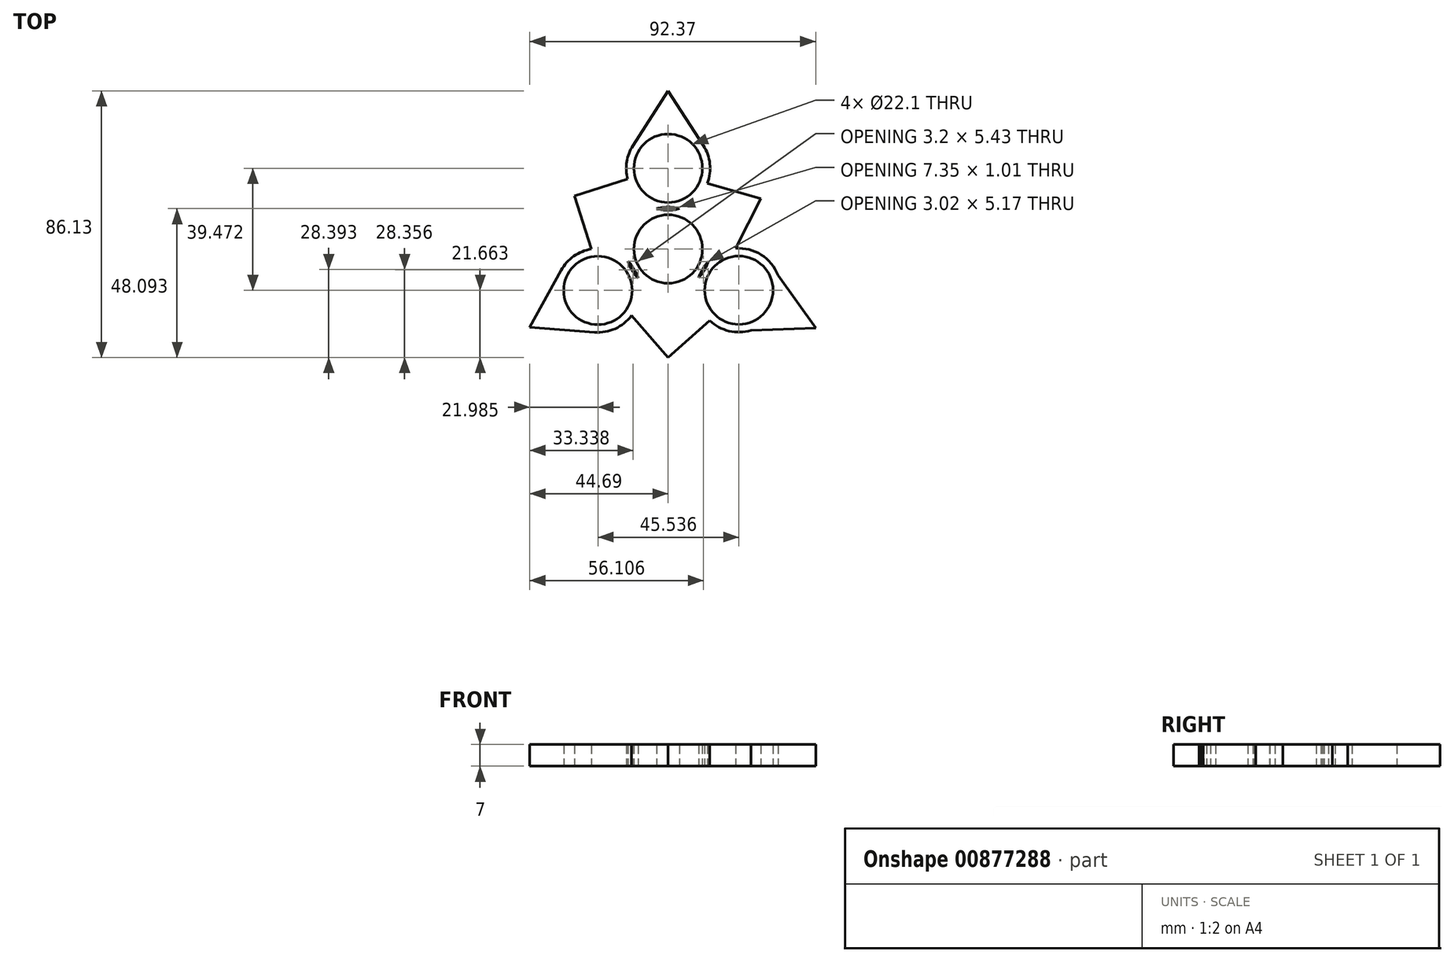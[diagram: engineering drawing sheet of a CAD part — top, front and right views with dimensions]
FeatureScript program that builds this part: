
annotation { "Feature Type Name" : "Feature", "Feature Type Description" : "" }
export const myFeature = defineFeature(function(context is Context, id is Id, definition is map)
    precondition{}
    {
        {
            var Q0;
            Q0=qCreatedBy(makeId("Top.planeOp"),FACE);
            var sketch = newSketch(context, id + "F0", { "sketchPlane" : qUnion([Q0])});
            skCircle(sketch, "E0", {"center": v(0, 0) * mm, "radius": 11.05 * mm});
            skCircle(sketch, "E1", {"center": v(0, 0) * mm, "radius": 13.55 * mm});
            skCircle(sketch, "E2", {"center": v(0, 26.09) * mm, "radius": 11.05 * mm});
            skCircle(sketch, "E3", {"center": v(0, 26.09) * mm, "radius": 13.55 * mm});
            skCircle(sketch, "E4.1.0", {"center": v(-22.7, -13.39) * mm, "radius": 11.05 * mm});
            skCircle(sketch, "E4.1.1", {"center": v(-22.7, -13.39) * mm, "radius": 13.55 * mm});
            skPoint(sketch, "E4.center", {"position": v(0.04, -0.2) * mm});
            skCircle(sketch, "E5.1.2.0", {"center": v(22.83, -13.31) * mm, "radius": 11.05 * mm});
            skCircle(sketch, "E5.2.2.0", {"center": v(22.83, -13.31) * mm, "radius": 13.55 * mm});
            skLineSegment(sketch, "E6", {"start": v(-11.39, 33.43) * mm, "end": v(0, 51.08) * mm});
            skLineSegment(sketch, "E7", {"start": v(0, 51.08) * mm, "end": v(11.39, 33.43) * mm});
            skLineSegment(sketch, "E8", {"start": v(-44.69, -25.27) * mm, "end": v(-34.58, -6.86) * mm});
            skLineSegment(sketch, "E9", {"start": v(-44.69, -25.27) * mm, "end": v(-23.75, -26.9) * mm});
            skLineSegment(sketch, "E10", {"start": v(-11.86, -21.5) * mm, "end": v(0, -35.05) * mm});
            skLineSegment(sketch, "E11", {"start": v(0, -35.05) * mm, "end": v(13.46, -23.1) * mm});
            skLineSegment(sketch, "E12", {"start": v(35.49, -8.47) * mm, "end": v(47.68, -25.56) * mm});
            skLineSegment(sketch, "E13", {"start": v(47.68, -25.56) * mm, "end": v(26.7, -26.3) * mm});
            skLineSegment(sketch, "E14", {"start": v(21.8, 0.2) * mm, "end": v(29.95, 16.24) * mm});
            skLineSegment(sketch, "E15", {"start": v(29.95, 16.24) * mm, "end": v(12.66, 21.25) * mm});
            skLineSegment(sketch, "E16", {"start": v(-24.8, 0) * mm, "end": v(-30.25, 17.16) * mm});
            skLineSegment(sketch, "E17", {"start": v(-30.25, 17.16) * mm, "end": v(-13.1, 22.6) * mm});
            skSolve(sketch);
        }
        {
            var Q0;
            {var subQ0=sQuery(id+"F0.wireOp",EDGE,"E16");Q0=makeQuery(id+"F0.imprint","IMPRINT",FACE,{"disambiguationData":[TD([[makeQuery(id+"F0.imprint","IMPRINT",EDGE,{"derivedFrom":subQ0}),-1.0]])]});}
            var Q1;
            {var subQ6=sQuery(id+"F0.wireOp",EDGE,"E10");Q1=makeQuery(id+"F0.imprint","IMPRINT",FACE,{"disambiguationData":[TD([[makeQuery(id+"F0.imprint","IMPRINT",EDGE,{"derivedFrom":subQ6}),1.0]])]});}
            var Q2;
            {var subQ0=sQuery(id+"F0.wireOp",EDGE,"E14");Q2=makeQuery(id+"F0.imprint","IMPRINT",FACE,{"disambiguationData":[TD([[makeQuery(id+"F0.imprint","IMPRINT",EDGE,{"derivedFrom":subQ0}),1.0]])]});}
            var Q3;
            Q3=makeQuery(id+"F0.imprint","IMPRINT",FACE,{"disambiguationData":[TD([[makeQuery(id+"F0.imprint","IMPRINT",EDGE,{"derivedFrom":sQuery(id+"F0.wireOp",EDGE,"E0")}),-1.0]])]});
            var Q4;
            Q4=makeQuery(id+"F0.imprint","IMPRINT",FACE,{"disambiguationData":[TD([[makeQuery(id+"F0.imprint","IMPRINT",EDGE,{"derivedFrom":sQuery(id+"F0.wireOp",EDGE,"E5.1.2.0")}),-1.0]])]});
            var Q5;
            {var subQ0=sQuery(id+"F0.wireOp",EDGE,"E12");Q5=makeQuery(id+"F0.imprint","IMPRINT",FACE,{"disambiguationData":[TD([[makeQuery(id+"F0.imprint","IMPRINT",EDGE,{"derivedFrom":subQ0}),-1.0]])]});}
            var Q6;
            Q6=makeQuery(id+"F0.imprint","IMPRINT",FACE,{"disambiguationData":[TD([[makeQuery(id+"F0.imprint","IMPRINT",EDGE,{"derivedFrom":sQuery(id+"F0.wireOp",EDGE,"E4.1.0")}),-1.0]])]});
            var Q7;
            {var subQ0=sQuery(id+"F0.wireOp",EDGE,"E8");Q7=makeQuery(id+"F0.imprint","IMPRINT",FACE,{"disambiguationData":[TD([[makeQuery(id+"F0.imprint","IMPRINT",EDGE,{"derivedFrom":subQ0}),-1.0]])]});}
            var Q8;
            {var subQ0=sQuery(id+"F0.wireOp",EDGE,"E6");Q8=makeQuery(id+"F0.imprint","IMPRINT",FACE,{"disambiguationData":[TD([[makeQuery(id+"F0.imprint","IMPRINT",EDGE,{"derivedFrom":subQ0}),-1.0]])]});}
            var Q9;
            Q9=makeQuery(id+"F0.imprint","IMPRINT",FACE,{"disambiguationData":[TD([[makeQuery(id+"F0.imprint","IMPRINT",EDGE,{"derivedFrom":sQuery(id+"F0.wireOp",EDGE,"E2")}),-1.0]])]});
            extrude(context, id + "F1", {"entities" : qUnion([Q0, Q1, Q2, Q3, Q4, Q5, Q6, Q7, Q8, Q9]), "depth" : 7 * mm, "offsetDistance" : 25 * mm});
        }
    });
